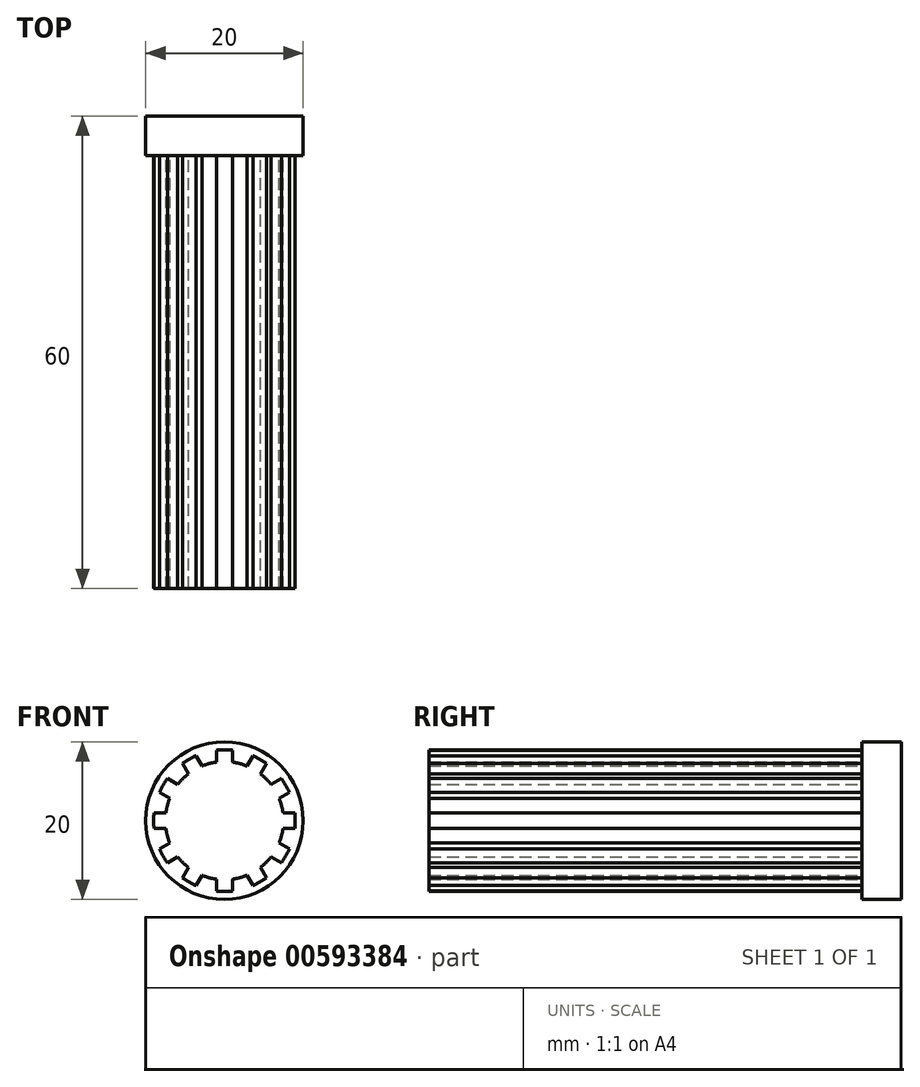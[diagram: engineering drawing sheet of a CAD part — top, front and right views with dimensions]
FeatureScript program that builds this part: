
annotation { "Feature Type Name" : "Feature", "Feature Type Description" : "" }
export const myFeature = defineFeature(function(context is Context, id is Id, definition is map)
    precondition{}
    {
        {
            var Q0;
            Q0=qCreatedBy(makeId("Front.planeOp"),FACE);
            var sketch = newSketch(context, id + "F0", { "sketchPlane" : qUnion([Q0])});
            skCircle(sketch, "E0", {"center": v(0, 0) * mm, "radius": 10 * mm});
            skArc(sketch, "E1", {"start": v(1, 8.94) * mm, "mid": v(0, 9) * mm, "end": v(-1, 8.94) * mm});
            skCircle(sketch, "E2", {"center": v(0, 0) * mm, "radius": 7.5 * mm});
            skLineSegment(sketch, "E3", {"start": v(-1, 8.94) * mm, "end": v(-1, 7.43) * mm});
            skLineSegment(sketch, "E4", {"start": v(1, 7.43) * mm, "end": v(1, 8.94) * mm});
            skLineSegment(sketch, "E5.1.0", {"start": v(-5.34, 7.25) * mm, "end": v(-4.58, 5.94) * mm});
            skArc(sketch, "E5.1.1", {"start": v(-3.6, 8.25) * mm, "mid": v(-4.5, 7.8) * mm, "end": v(-5.34, 7.25) * mm});
            skLineSegment(sketch, "E5.1.2", {"start": v(-2.85, 6.94) * mm, "end": v(-3.6, 8.25) * mm});
            skLineSegment(sketch, "E5.2.0", {"start": v(-8.25, 3.6) * mm, "end": v(-6.94, 2.85) * mm});
            skArc(sketch, "E5.2.1", {"start": v(-7.25, 5.34) * mm, "mid": v(-7.8, 4.5) * mm, "end": v(-8.25, 3.6) * mm});
            skLineSegment(sketch, "E5.2.2", {"start": v(-5.94, 4.58) * mm, "end": v(-7.25, 5.34) * mm});
            skLineSegment(sketch, "E5.3.0", {"start": v(-8.94, -1) * mm, "end": v(-7.43, -1) * mm});
            skArc(sketch, "E5.3.1", {"start": v(-8.94, 1) * mm, "mid": v(-9, 0) * mm, "end": v(-8.94, -1) * mm});
            skLineSegment(sketch, "E5.3.2", {"start": v(-7.43, 1) * mm, "end": v(-8.94, 1) * mm});
            skLineSegment(sketch, "E5.4.0", {"start": v(-7.25, -5.34) * mm, "end": v(-5.94, -4.58) * mm});
            skArc(sketch, "E5.4.1", {"start": v(-8.25, -3.6) * mm, "mid": v(-7.8, -4.5) * mm, "end": v(-7.25, -5.34) * mm});
            skLineSegment(sketch, "E5.4.2", {"start": v(-6.94, -2.85) * mm, "end": v(-8.25, -3.6) * mm});
            skLineSegment(sketch, "E5.5.0", {"start": v(-3.6, -8.25) * mm, "end": v(-2.85, -6.94) * mm});
            skArc(sketch, "E5.5.1", {"start": v(-5.34, -7.25) * mm, "mid": v(-4.5, -7.8) * mm, "end": v(-3.6, -8.25) * mm});
            skLineSegment(sketch, "E5.5.2", {"start": v(-4.58, -5.94) * mm, "end": v(-5.34, -7.25) * mm});
            skLineSegment(sketch, "E5.6.0", {"start": v(1, -8.94) * mm, "end": v(1, -7.43) * mm});
            skArc(sketch, "E5.6.1", {"start": v(-1, -8.94) * mm, "mid": v(0, -9) * mm, "end": v(1, -8.94) * mm});
            skLineSegment(sketch, "E5.6.2", {"start": v(-1, -7.43) * mm, "end": v(-1, -8.94) * mm});
            skLineSegment(sketch, "E5.7.0", {"start": v(5.34, -7.25) * mm, "end": v(4.58, -5.94) * mm});
            skArc(sketch, "E5.7.1", {"start": v(3.6, -8.25) * mm, "mid": v(4.5, -7.8) * mm, "end": v(5.34, -7.25) * mm});
            skLineSegment(sketch, "E5.7.2", {"start": v(2.85, -6.94) * mm, "end": v(3.6, -8.25) * mm});
            skLineSegment(sketch, "E5.8.0", {"start": v(8.25, -3.6) * mm, "end": v(6.94, -2.85) * mm});
            skArc(sketch, "E5.8.1", {"start": v(7.25, -5.34) * mm, "mid": v(7.8, -4.5) * mm, "end": v(8.25, -3.6) * mm});
            skLineSegment(sketch, "E5.8.2", {"start": v(5.94, -4.58) * mm, "end": v(7.25, -5.34) * mm});
            skLineSegment(sketch, "E5.9.0", {"start": v(8.94, 1) * mm, "end": v(7.43, 1) * mm});
            skArc(sketch, "E5.9.1", {"start": v(8.94, -1) * mm, "mid": v(9, 0) * mm, "end": v(8.94, 1) * mm});
            skLineSegment(sketch, "E5.9.2", {"start": v(7.43, -1) * mm, "end": v(8.94, -1) * mm});
            skLineSegment(sketch, "E5.10.0", {"start": v(7.25, 5.34) * mm, "end": v(5.94, 4.58) * mm});
            skArc(sketch, "E5.10.1", {"start": v(8.25, 3.6) * mm, "mid": v(7.8, 4.5) * mm, "end": v(7.25, 5.34) * mm});
            skLineSegment(sketch, "E5.10.2", {"start": v(6.94, 2.85) * mm, "end": v(8.25, 3.6) * mm});
            skLineSegment(sketch, "E5.11.0", {"start": v(3.6, 8.25) * mm, "end": v(2.85, 6.94) * mm});
            skArc(sketch, "E5.11.1", {"start": v(5.34, 7.25) * mm, "mid": v(4.5, 7.8) * mm, "end": v(3.6, 8.25) * mm});
            skLineSegment(sketch, "E5.11.2", {"start": v(4.58, 5.94) * mm, "end": v(5.34, 7.25) * mm});
            skSolve(sketch);
        }
        {
            var Q0;
            Q0=makeQuery(id+"F0.imprint","IMPRINT",FACE,{"disambiguationData":[TD([[makeQuery(id+"F0.imprint","IMPRINT",EDGE,{"derivedFrom":sQuery(id+"F0.wireOp",EDGE,"E1")}),1.0]])]});
            var Q1;
            {var subQ0=sQuery(id+"F0.wireOp",EDGE,"E5.11.0");Q1=makeQuery(id+"F0.imprint","IMPRINT",FACE,{"disambiguationData":[TD([[makeQuery(id+"F0.imprint","IMPRINT",EDGE,{"derivedFrom":subQ0}),1.0]])]});}
            var Q2;
            {var subQ0=sQuery(id+"F0.wireOp",EDGE,"E5.10.0");Q2=makeQuery(id+"F0.imprint","IMPRINT",FACE,{"disambiguationData":[TD([[makeQuery(id+"F0.imprint","IMPRINT",EDGE,{"derivedFrom":subQ0}),1.0]])]});}
            var Q3;
            {var subQ0=sQuery(id+"F0.wireOp",EDGE,"E5.9.0");Q3=makeQuery(id+"F0.imprint","IMPRINT",FACE,{"disambiguationData":[TD([[makeQuery(id+"F0.imprint","IMPRINT",EDGE,{"derivedFrom":subQ0}),1.0]])]});}
            var Q4;
            {var subQ0=sQuery(id+"F0.wireOp",EDGE,"E5.8.0");Q4=makeQuery(id+"F0.imprint","IMPRINT",FACE,{"disambiguationData":[TD([[makeQuery(id+"F0.imprint","IMPRINT",EDGE,{"derivedFrom":subQ0}),1.0]])]});}
            var Q5;
            {var subQ0=sQuery(id+"F0.wireOp",EDGE,"E5.7.0");Q5=makeQuery(id+"F0.imprint","IMPRINT",FACE,{"disambiguationData":[TD([[makeQuery(id+"F0.imprint","IMPRINT",EDGE,{"derivedFrom":subQ0}),1.0]])]});}
            var Q6;
            {var subQ0=sQuery(id+"F0.wireOp",EDGE,"E5.6.0");Q6=makeQuery(id+"F0.imprint","IMPRINT",FACE,{"disambiguationData":[TD([[makeQuery(id+"F0.imprint","IMPRINT",EDGE,{"derivedFrom":subQ0}),1.0]])]});}
            var Q7;
            {var subQ0=sQuery(id+"F0.wireOp",EDGE,"E5.5.0");Q7=makeQuery(id+"F0.imprint","IMPRINT",FACE,{"disambiguationData":[TD([[makeQuery(id+"F0.imprint","IMPRINT",EDGE,{"derivedFrom":subQ0}),1.0]])]});}
            var Q8;
            {var subQ0=sQuery(id+"F0.wireOp",EDGE,"E5.4.0");Q8=makeQuery(id+"F0.imprint","IMPRINT",FACE,{"disambiguationData":[TD([[makeQuery(id+"F0.imprint","IMPRINT",EDGE,{"derivedFrom":subQ0}),1.0]])]});}
            var Q9;
            {var subQ0=sQuery(id+"F0.wireOp",EDGE,"E5.3.0");Q9=makeQuery(id+"F0.imprint","IMPRINT",FACE,{"disambiguationData":[TD([[makeQuery(id+"F0.imprint","IMPRINT",EDGE,{"derivedFrom":subQ0}),1.0]])]});}
            var Q10;
            {var subQ0=sQuery(id+"F0.wireOp",EDGE,"E5.2.0");Q10=makeQuery(id+"F0.imprint","IMPRINT",FACE,{"disambiguationData":[TD([[makeQuery(id+"F0.imprint","IMPRINT",EDGE,{"derivedFrom":subQ0}),1.0]])]});}
            var Q11;
            {var subQ0=sQuery(id+"F0.wireOp",EDGE,"E5.1.0");Q11=makeQuery(id+"F0.imprint","IMPRINT",FACE,{"disambiguationData":[TD([[makeQuery(id+"F0.imprint","IMPRINT",EDGE,{"derivedFrom":subQ0}),1.0]])]});}
            var Q12;
            {var subQ0=sQuery(id+"F0.wireOp",EDGE,"E2");var subQ18=makeQuery(id+"F0.imprint","INTERSECT",VERTEX,{"derivedFrom":[subQ0,sQuery(id+"F0.wireOp",EDGE,"E5.9.0")]});Q12=makeQuery(id+"F0.imprint","IMPRINT",FACE,{"disambiguationData":[TD([[makeQuery(id+"F0.imprint","IMPRINT",EDGE,{"disambiguationData":[TD([[subQ18,-1.0]])],"derivedFrom":subQ0}),1.0]])]});}
            extrude(context, id + "F1", {"entities" : qUnion([Q0, Q1, Q2, Q3, Q4, Q5, Q6, Q7, Q8, Q9, Q10, Q11, Q12]), "depth" : 60 * mm, "offsetDistance" : 25 * mm});
        }
        {
            var Q0;
            Q0=makeQuery(id+"F0.imprint","IMPRINT",FACE,{"disambiguationData":[TD([[makeQuery(id+"F0.imprint","IMPRINT",EDGE,{"derivedFrom":sQuery(id+"F0.wireOp",EDGE,"E0")}),1.0]])]});
            var Q1;
            {var subQ0=sQuery(id+"F0.wireOp",EDGE,"E2");var subQ18=makeQuery(id+"F0.imprint","INTERSECT",VERTEX,{"derivedFrom":[subQ0,sQuery(id+"F0.wireOp",EDGE,"E5.9.0")]});Q1=makeQuery(id+"F0.imprint","IMPRINT",FACE,{"disambiguationData":[TD([[makeQuery(id+"F0.imprint","IMPRINT",EDGE,{"disambiguationData":[TD([[subQ18,-1.0]])],"derivedFrom":subQ0}),1.0]])]});}
            var Q2;
            {var subQ0=sQuery(id+"F0.wireOp",EDGE,"E5.6.0");Q2=makeQuery(id+"F0.imprint","IMPRINT",FACE,{"disambiguationData":[TD([[makeQuery(id+"F0.imprint","IMPRINT",EDGE,{"derivedFrom":subQ0}),1.0]])]});}
            var Q3;
            {var subQ0=sQuery(id+"F0.wireOp",EDGE,"E5.7.0");Q3=makeQuery(id+"F0.imprint","IMPRINT",FACE,{"disambiguationData":[TD([[makeQuery(id+"F0.imprint","IMPRINT",EDGE,{"derivedFrom":subQ0}),1.0]])]});}
            var Q4;
            {var subQ0=sQuery(id+"F0.wireOp",EDGE,"E5.8.0");Q4=makeQuery(id+"F0.imprint","IMPRINT",FACE,{"disambiguationData":[TD([[makeQuery(id+"F0.imprint","IMPRINT",EDGE,{"derivedFrom":subQ0}),1.0]])]});}
            var Q5;
            {var subQ0=sQuery(id+"F0.wireOp",EDGE,"E5.9.0");Q5=makeQuery(id+"F0.imprint","IMPRINT",FACE,{"disambiguationData":[TD([[makeQuery(id+"F0.imprint","IMPRINT",EDGE,{"derivedFrom":subQ0}),1.0]])]});}
            var Q6;
            {var subQ0=sQuery(id+"F0.wireOp",EDGE,"E5.10.0");Q6=makeQuery(id+"F0.imprint","IMPRINT",FACE,{"disambiguationData":[TD([[makeQuery(id+"F0.imprint","IMPRINT",EDGE,{"derivedFrom":subQ0}),1.0]])]});}
            var Q7;
            {var subQ0=sQuery(id+"F0.wireOp",EDGE,"E5.11.0");Q7=makeQuery(id+"F0.imprint","IMPRINT",FACE,{"disambiguationData":[TD([[makeQuery(id+"F0.imprint","IMPRINT",EDGE,{"derivedFrom":subQ0}),1.0]])]});}
            var Q8;
            Q8=makeQuery(id+"F0.imprint","IMPRINT",FACE,{"disambiguationData":[TD([[makeQuery(id+"F0.imprint","IMPRINT",EDGE,{"derivedFrom":sQuery(id+"F0.wireOp",EDGE,"E1")}),1.0]])]});
            var Q9;
            {var subQ0=sQuery(id+"F0.wireOp",EDGE,"E5.1.0");Q9=makeQuery(id+"F0.imprint","IMPRINT",FACE,{"disambiguationData":[TD([[makeQuery(id+"F0.imprint","IMPRINT",EDGE,{"derivedFrom":subQ0}),1.0]])]});}
            var Q10;
            {var subQ0=sQuery(id+"F0.wireOp",EDGE,"E5.2.0");Q10=makeQuery(id+"F0.imprint","IMPRINT",FACE,{"disambiguationData":[TD([[makeQuery(id+"F0.imprint","IMPRINT",EDGE,{"derivedFrom":subQ0}),1.0]])]});}
            var Q11;
            {var subQ0=sQuery(id+"F0.wireOp",EDGE,"E5.3.0");Q11=makeQuery(id+"F0.imprint","IMPRINT",FACE,{"disambiguationData":[TD([[makeQuery(id+"F0.imprint","IMPRINT",EDGE,{"derivedFrom":subQ0}),1.0]])]});}
            var Q12;
            {var subQ0=sQuery(id+"F0.wireOp",EDGE,"E5.4.0");Q12=makeQuery(id+"F0.imprint","IMPRINT",FACE,{"disambiguationData":[TD([[makeQuery(id+"F0.imprint","IMPRINT",EDGE,{"derivedFrom":subQ0}),1.0]])]});}
            var Q13;
            {var subQ0=sQuery(id+"F0.wireOp",EDGE,"E5.5.0");Q13=makeQuery(id+"F0.imprint","IMPRINT",FACE,{"disambiguationData":[TD([[makeQuery(id+"F0.imprint","IMPRINT",EDGE,{"derivedFrom":subQ0}),1.0]])]});}
            extrude(context, id + "F2", {"entities" : qUnion([Q0, Q1, Q2, Q3, Q4, Q5, Q6, Q7, Q8, Q9, Q10, Q11, Q12, Q13]), "operationType" : NewBodyOperationType.ADD, "depth" : 5 * mm, "offsetDistance" : 25 * mm});
        }
    });
